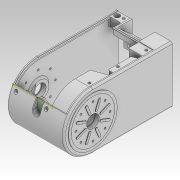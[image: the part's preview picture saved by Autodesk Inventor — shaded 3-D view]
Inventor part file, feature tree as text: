
AUTODESK INVENTOR PART (.ipt)
format: ipt  version: 2020 (Build 240168000, 168)  size: 1,219,584 bytes
history: native  units: mm
features: extrude x55, sketch x55, projected_geometry x9, fillet x8, plane x7, chamfer x5, pattern_circular x2, revolve x2, loft x1, other x1
ambient origin geometry x8: Origin, YZ Plane, XZ Plane, XY Plane, X Axis, Y Axis, Z Axis, Center Point
bodies: Solid1 (feature_tree)
feature tree (145):
  extrude  "Extrusion1"  Depth=250.0mm
  extrude  "Extrusion2"  Depth=100.0mm TaperAngle=0.0deg
  extrude  "Extrusion3"  TaperAngle=0.0deg  [1 undecoded]
  extrude  "Extrusion4"  Depth=10.0mm
  extrude  "Extrusion5"  Depth=30.0mm
  pattern_circular  "Circular Pattern1"  Count=8 Angle=360.0deg
  plane  "Work Plane1"
  plane  "Work Plane2"
  extrude  "Extrusion6"  Depth=30.0mm
  extrude  "Extrusion7"  Depth=10.0mm
  extrude  "Extrusion8"  Depth=10.0mm
  extrude  "Extrusion9"  [1 undecoded]
  chamfer  "Chamfer1"  Distance=10.0mm
  extrude  "Extrusion13"  Depth=10.0mm TaperAngle=0.0deg
  extrude  "Extrusion14"  Depth=3.0mm TaperAngle=0.0deg
  extrude  "Extrusion15"  Depth=3.0mm
  extrude  "Extrusion16"  Depth=3.0mm
  extrude  "Extrusion17"  Depth=80.0mm
  extrude  "Extrusion18"  Depth=60.0mm
  extrude  "Extrusion19"  Depth=80.0mm TaperAngle=360.0deg
  extrude  "Extrusion20"  Depth=15.5mm TaperAngle=0.0deg
  fillet  "Fillet2"  Radius=22.1mm
  pattern_circular  "Circular Pattern2"  Count=8 Angle=360.0deg
  extrude  "Extrusion21"  Depth=10.0mm
  extrude  "Extrusion22"  Depth=7.0mm
  plane  "Work Plane3"
  revolve  "Revolution1"  [1 undecoded]
  revolve  "Revolution2"  [1 undecoded]
  plane  "Work Plane4"
  extrude  "Extrusion23"  Depth=96.8mm TaperAngle=0.0deg
  extrude  "Extrusion24"  Depth=2.5mm
  fillet  "Fillet3"  Radius=5.2mm
  loft  "Loft1"
  extrude  "Extrusion25"  TaperAngle=90.0deg  [1 undecoded]
  extrude  "Extrusion26"  Depth=15.0mm
  extrude  "Extrusion27"  Depth=19.0mm
  extrude  "Extrusion28"  Depth=2.7mm
  plane  "Work Plane5"
  extrude  "Extrusion29"  Depth=4.0mm
  extrude  "Extrusion30"  TaperAngle=90.0deg  [1 undecoded]
  extrude  "Extrusion32"  Depth=18.8mm TaperAngle=0.0deg
  extrude  "Extrusion35"  Depth=6.0mm
  extrude  "Extrusion36"  Depth=4.0mm
  extrude  "Extrusion37"  [1 undecoded]
  chamfer  "Chamfer3"  Distance=1.0mm
  plane  "Work Plane8"
  extrude  "Extrusion38"  Depth=5.0mm
  extrude  "Extrusion39"  TaperAngle=0.0deg  [1 undecoded]
  fillet  "Fillet5"  [1 undecoded]
  extrude  "Extrusion40"  Depth=10.0mm TaperAngle=0.0deg
  chamfer  "Chamfer4"  [1 undecoded]
  chamfer  "Chamfer5"  Distance=255.0mm
  extrude  "Extrusion41"  Depth=5.0mm
  extrude  "Extrusion42"  Depth=12.0mm
  chamfer  "Chamfer6"  Distance=64.0mm
  fillet  "Fillet6"  Radius=3.0mm
  fillet  "Fillet7"  Radius=5.0mm
  extrude  "Extrusion43"  Depth=5.0mm
  extrude  "Extrusion44"  Depth=3.0mm
  extrude  "Extrusion45"  Depth=10.0mm TaperAngle=0.0deg
  extrude  "Extrusion46"  Depth=3.0mm TaperAngle=45.0deg
  extrude  "Extrusion47"  Depth=3.0mm
  extrude  "Extrusion48"  Depth=0.25mm
  fillet  "Fillet8"  Radius=17.25mm
  extrude  "Extrusion49"  Depth=3.0mm
  extrude  "Extrusion50"  Depth=15.0mm
  extrude  "Extrusion51"  Depth=3.0mm
  fillet  "Fillet9"  Radius=3.8mm
  extrude  "Extrusion52"  Depth=3.0mm TaperAngle=0.0deg
  extrude  "Extrusion54"  Depth=3.0mm
  sketch  "Sketch62"  dims[d155=110.0mm d156=0.0mm d157=0.0mm]
  extrude  "Extrusion55"  Depth=3.0mm TaperAngle=0.0deg
  extrude  "Extrusion56"  Depth=3.0mm
  extrude  "Extrusion57"  Depth=3.0mm
  extrude  "Extrusion58"  Depth=3.0mm
  plane  "Work Plane10"
  extrude  "Extrusion59"  Depth=3.0mm
  extrude  "Extrusion60"  Depth=3.0mm TaperAngle=0.0deg
  extrude  "Extrusion61"  Depth=3.0mm
  fillet  "Fillet10"  Radius=2.0mm
  extrude  "Extrusion62"  Depth=3.0mm
  sketch  "Sketch1"  dims[d0=50.0mm d1=250.0mm]
  sketch  "Sketch2"  dims[d2=50.0mm d3=100.0mm d4=0.0mm]
  sketch  "Sketch4"  dims[d5=5.0mm d7=0.0mm d8=0.0mm]
  sketch  "Sketch5"  dims[d11=10.0mm d12=0.0mm d14=85.0mm]
  sketch  "Sketch7"  dims[d15=1.0mm d16=0.0mm d17=30.0mm]
  projected_geometry  "Projected Loop1"
  sketch  "Sketch8"  dims[d18=3.3mm]
  projected_geometry  "Projected Loop2"
  projected_geometry  "Projected Loop4"
  sketch  "Sketch9"  dims[d19=15.0mm d20=0.0mm d21=80.0mm d22=360.0deg]
  sketch  "Sketch10"  dims[d24=30.0mm d25=30.0mm]
  sketch  "Sketch14"  dims[d30=-5.0mm d31=10.0mm]
  sketch  "Sketch15"  dims[d32=10.0mm d33=10.0mm]
  sketch  "Sketch16"  dims[d34=31.5mm d35=0.0mm d36=-5.0mm d38=10.0mm d39=0.0mm]
  sketch  "Sketch17"  dims[d40=22.1mm d41=10.0mm d42=0.0mm]
  sketch  "Sketch18"  dims[d43=5.0mm d44=3.0mm d45=0.0mm]
  sketch  "Sketch19"  dims[d56=3.0mm d57=2.0mm d58=45.0deg d62=95.1mm]
  sketch  "Sketch20"  dims[d63=10.0mm d64=0.0mm d65=3.0mm]
  sketch  "Sketch21"  dims[d66=0.5mm d67=0.0mm d68=80.0mm]
  sketch  "Sketch22"  dims[d69=15.5mm d70=0.0mm d71=60.0mm]
  sketch  "Sketch23"  dims[d72=3.2mm d73=80.0mm d75=360.0deg]
  other  "Work Axis1"
  sketch  "Sketch24"  dims[d77=15.5mm d78=0.0mm d79=15.5mm d80=0.0mm d81=22.1mm]
  projected_geometry  "Projected Loop5"
  projected_geometry  "Projected Loop6"
  sketch  "Sketch26"  dims[d82=0.0mm d83=0.0mm]
  sketch  "Sketch27"  dims[d84=76.0mm]
  sketch  "Sketch28"  dims[d85=0.1mm d86=0.0mm]
  sketch  "Sketch29"  dims[d87=15.0mm]
  sketch  "Sketch30"  dims[d88=2.0mm]
  sketch  "Sketch31"  dims[d89=22.5mm]
  sketch  "Sketch32"  dims[d90=0.8mm d91=0.0mm]
  sketch  "Sketch33"  dims[d92=0.2mm d93=80.0mm d94=360.0deg]
  projected_geometry  "Projected Loop7"
  sketch  "Sketch34"  dims[d96=24.43461mm d97=10.0mm]
  sketch  "Sketch35"  dims[d98=6.1mm d99=7.0mm]
  sketch  "Sketch38"  dims[d100=6.1mm d101=7.0mm]
  projected_geometry  "Projected Loop8"
  sketch  "Sketch42"  dims[d102=5.0mm d103=0.0mm d104=25.0mm]
  sketch  "Sketch43"  dims[d105=16.1mm d106=96.8mm d107=0.0mm]
  sketch  "Sketch45"  dims[d108=0.0mm d109=2.5mm d110=5.2mm]
  projected_geometry  "Projected Loop9"
  sketch  "Sketch46"  dims[d111=1.0mm d112=5.0mm]
  sketch  "Sketch47"  dims[d113=5.2mm d114=90.0deg]
  sketch  "Sketch48"  dims[d115=15.0mm d116=25.0mm]
  sketch  "Sketch49"  dims[d117=25.0mm d118=19.0mm]
  sketch  "Sketch50"  dims[d119=19.0mm d120=2.7mm]
  projected_geometry  "Projected Loop10"
  sketch  "Sketch51"  dims[d122=4.0mm d123=0.0mm d124=5.5mm]
  sketch  "Sketch52"  dims[d125=2.0mm d126=0.0mm d127=90.0deg]
  sketch  "Sketch53"  dims[d128=2.0mm d129=18.8mm d130=0.0mm]
  sketch  "Sketch54"  dims[d131=111.25mm d132=0.0mm d133=6.0mm]
  sketch  "Sketch55"  dims[d134=4.0mm d135=0.0mm d136=1.0mm]
  sketch  "Sketch56"  dims[d137=1.0mm d138=0.0mm d139=-7.0mm]
  sketch  "Sketch57"  dims[d140=1.0mm d141=1.0mm d142=0.0mm]
  sketch  "Sketch58"  dims[d143=7.0mm d144=5.0mm]
  sketch  "Sketch59"  dims[d145=6.0mm d146=0.0mm d147=90.0deg d148=0.0mm d149=90.0deg]
  sketch  "Sketch61"  dims[d150=3.0mm d151=10.0mm d152=0.0mm]
  sketch  "Sketch63"  dims[d159=30.0deg]
  sketch  "Sketch64"  dims[d160=6.0mm d177=255.0mm d178=0.0mm]
  sketch  "Sketch65"  dims[d179=2.1mm d180=5.0mm]
  sketch  "Sketch66"  dims[d181=42.0mm d182=0.0mm d183=12.0mm]
  sketch  "Sketch67"  dims[d184=78.0mm]
  sketch  "Sketch68"  dims[d185=45.0mm d186=64.0mm d187=3.0mm d188=0.0mm d189=5.0mm d190=5.0mm d191=4.3mm d192=10.0mm d193=0.0mm d194=3.0mm d195=2.0mm d196=45.0deg d199=23.0mm d200=0.25mm d201=17.25mm d202=0.0mm d203=58.0mm d204=15.0mm d205=61.8mm d206=3.8mm d207=8.0mm d208=0.0mm d209=2.0mm d210=20.75mm d211=0.0mm d212=1.0mm d213=7.0mm d214=2.0mm d215=3.490659mm d216=7.0mm d217=2.0mm d218=3.490659mm d219=1.0mm d220=90.0mm d221=0.0mm d222=2.0mm d223=2.0mm d224=0.0mm d225=2.0mm d226=2.0mm d227=3.490659mm d228=2.0mm d229=3.0mm d230=2.0mm d231=10.0mm d232=0.0mm d233=2.0mm d234=0.5mm d235=45.0deg d236=10.0mm d237=0.0mm d238=5.0mm d239=10.0mm d240=10.0mm d241=0.0mm d242=30.0mm d243=3.5mm d244=12.0mm d245=10.0mm d246=0.0mm d247=5.5mm d248=3.0mm d249=0.0mm d250=30.0mm d251=6.0mm d252=10.0mm d253=0.0mm d254=1.0mm d255=15.0mm d256=15.0mm d257=10.0mm d258=0.0mm d259=4.0mm d260=5.5mm d261=10.0mm d262=0.0mm d263=9.0mm d264=5.0mm d265=0.0mm d266=2.0mm d267=0.2mm d268=0.0mm d274=58.0mm d275=58.0mm d276=9.0mm d277=9.0mm d278=9.0mm d279=9.0mm d280=9.0mm d281=9.0mm d282=9.0mm d283=9.0mm d284=0.5mm d285=15.0mm d286=0.0mm d287=7.0mm d288=3.5mm d289=5.0mm d290=0.0mm d291=5.0mm d292=0.0mm d293=6.0mm d294=6.0mm d295=6.0mm d296=6.0mm d297=6.0mm d298=4.3mm d299=10.0mm d300=0.0mm d301=6.0mm d302=6.0mm d303=6.0mm d304=6.0mm d305=3.2mm d306=10.0mm d307=0.0mm d308=-2.5mm d309=6.0mm d310=10.0mm d311=0.0mm d312=3.490659mm d313=3.490659mm d314=10.0mm d315=0.0mm d316=10.0mm d317=0.0mm d318=3.0mm d319=0.2mm d320=0.0mm d321=53.0mm d322=0.872665mm]
note: 10 required parameter values undecoded (feature->parameter linkage not recoverable at this tier; creation-order binding heuristic only, values carry confidence <= 0.55)